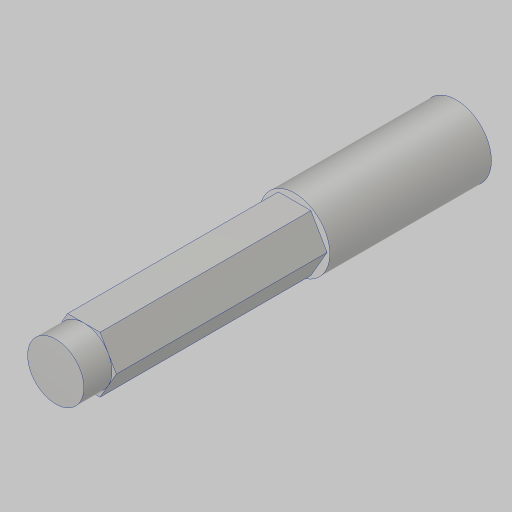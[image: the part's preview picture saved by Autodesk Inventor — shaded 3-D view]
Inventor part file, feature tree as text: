
AUTODESK INVENTOR PART (.ipt)
format: ipt  version: 2023.5 (Build 275446000, 446)  size: 125,952 bytes
history: native  units: in
note: dims shown in document units (in); Inventor stores cm internally (conversion verified against a paired STEP export)
features: extrude x3, sketch x3, projected_geometry x2
ambient origin geometry x8: Origin, YZ Plane, XZ Plane, XY Plane, X Axis, Y Axis, Z Axis, Center Point
bodies: Solid1 (feature_tree)
feature tree (8):
  extrude  "Extrusion1"  Depth=3.5625in TaperAngle=0.0deg
  extrude  "Extrusion2"  Depth=2.125in TaperAngle=0.0deg
  extrude  "Extrusion3"  Depth=0.25in TaperAngle=0.0deg
  sketch  "Sketch1"  dims[d0=0.625in d1=3.5625in d2=0.0in]
  sketch  "Sketch2"  dims[d3=0.5in d4=2.125in d5=0.0in]
  projected_geometry  "Projected Loop1"
  sketch  "Sketch3"  dims[d6=0.5in d7=0.25in d8=0.0in]
  projected_geometry  "Projected Loop2"
